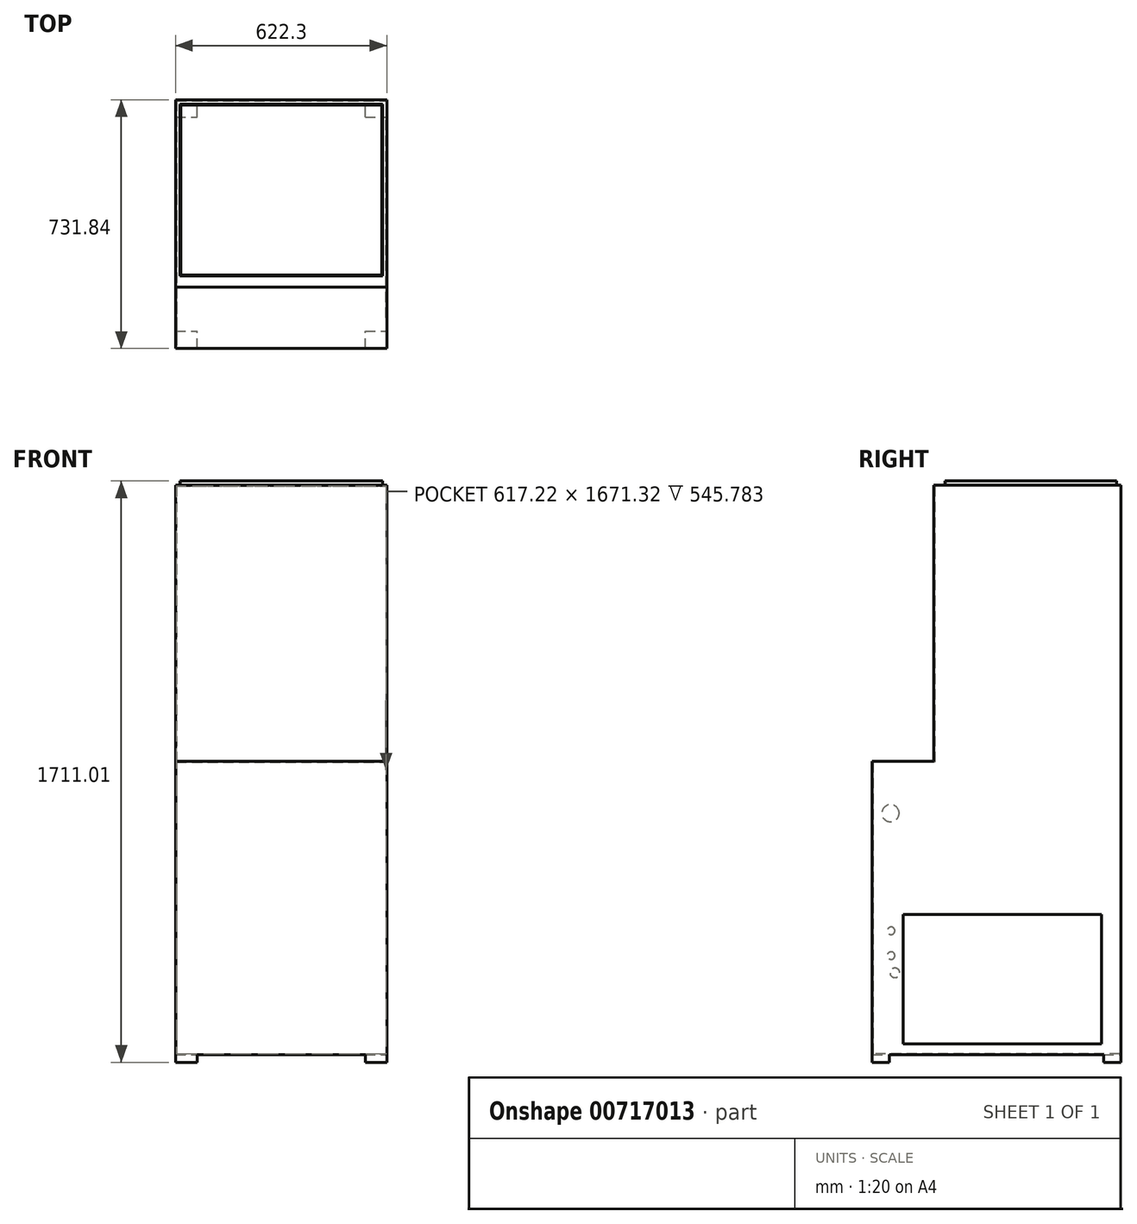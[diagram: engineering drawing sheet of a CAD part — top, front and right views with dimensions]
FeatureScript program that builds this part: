
annotation { "Feature Type Name" : "Feature", "Feature Type Description" : "" }
export const myFeature = defineFeature(function(context is Context, id is Id, definition is map)
    precondition{}
    {
        {
            var Q0;
            Q0=qCreatedBy(makeId("Top.planeOp"),FACE);
            var sketch = newSketch(context, id + "F0", { "sketchPlane" : qUnion([Q0])});
            skLineSegment(sketch, "E0.bottom", {"start": v(-311.15, 365.92) * mm, "end": v(311.15, 365.92) * mm});
            skLineSegment(sketch, "E0.top", {"start": v(-311.15, -365.92) * mm, "end": v(311.15, -365.92) * mm});
            skLineSegment(sketch, "E0.left", {"start": v(-311.15, 365.92) * mm, "end": v(-311.15, -365.92) * mm});
            skLineSegment(sketch, "E0.right", {"start": v(311.15, 365.92) * mm, "end": v(311.15, -365.92) * mm});
            skLineSegment(sketch, "E1", {"start": v(0, 0) * mm, "end": v(-311.15, 0) * mm, "construction": true});
            skLineSegment(sketch, "E2", {"start": v(0, 0) * mm, "end": v(0, 365.92) * mm, "construction": true});
            skSolve(sketch);
        }
        {
            var Q0;
            Q0=makeQuery(id+"F0.imprint","IMPRINT",FACE,{"disambiguationData":[TD([[makeQuery(id+"F0.imprint","IMPRINT",EDGE,{"derivedFrom":sQuery(id+"F0.wireOp",EDGE,"E0.bottom")}),-1.0]])]});
            extrude(context, id + "F1", {"entities" : qUnion([Q0]), "depth" : 863.6 * mm, "offsetDistance" : 25.4 * mm});
        }
        {
            var Q0;
            Q0=makeQuery(id+"F1.opExtrude","CAP_FACE",FACE,{"disambiguationData":[OSD([sQuery(id+"F0.wireOp",EDGE,"E0.bottom"),sQuery(id+"F0.wireOp",EDGE,"E0.top"),sQuery(id+"F0.wireOp",EDGE,"E0.left"),sQuery(id+"F0.wireOp",EDGE,"E0.right")])],"isStart":false});
            var sketch = newSketch(context, id + "F2", { "sketchPlane" : qUnion([Q0])});
            skLineSegment(sketch, "E3.bottom", {"start": v(-311.15, 365.92) * mm, "end": v(311.15, 365.92) * mm});
            skLineSegment(sketch, "E3.top", {"start": v(-311.15, -184.94) * mm, "end": v(311.15, -184.94) * mm});
            skLineSegment(sketch, "E3.left", {"start": v(-311.15, 365.92) * mm, "end": v(-311.15, -184.94) * mm});
            skLineSegment(sketch, "E3.right", {"start": v(311.15, 365.92) * mm, "end": v(311.15, -184.94) * mm});
            skSolve(sketch);
        }
        {
            var Q0;
            Q0=makeQuery(id+"F2.imprint","IMPRINT",FACE,{"disambiguationData":[TD([[makeQuery(id+"F2.imprint","IMPRINT",EDGE,{"derivedFrom":sQuery(id+"F2.wireOp",EDGE,"E3.bottom")}),-1.0]])]});
            extrude(context, id + "F3", {"entities" : qUnion([Q0]), "operationType" : NewBodyOperationType.ADD, "depth" : 812.8 * mm, "offsetDistance" : 25.4 * mm});
        }
        {
            var Q0;
            Q0=makeQuery(id+"F3.opExtrude","CAP_FACE",FACE,{"disambiguationData":[OSD([sQuery(id+"F2.wireOp",EDGE,"E3.bottom"),sQuery(id+"F2.wireOp",EDGE,"E3.top"),sQuery(id+"F2.wireOp",EDGE,"E3.left"),sQuery(id+"F2.wireOp",EDGE,"E3.right")])],"isStart":false});
            var sketch = newSketch(context, id + "F4", { "sketchPlane" : qUnion([Q0])});
            skLineSegment(sketch, "E4.bottom", {"start": v(-298.45, 353.22) * mm, "end": v(298.45, 353.22) * mm});
            skLineSegment(sketch, "E4.top", {"start": v(-298.45, -151.6) * mm, "end": v(298.45, -151.6) * mm});
            skLineSegment(sketch, "E4.left", {"start": v(-298.45, 353.22) * mm, "end": v(-298.45, -151.6) * mm});
            skLineSegment(sketch, "E4.right", {"start": v(298.45, 353.22) * mm, "end": v(298.45, -151.6) * mm});
            skLineSegment(sketch, "E5.0", {"start": v(295.91, 350.68) * mm, "end": v(295.91, -149.07) * mm});
            skLineSegment(sketch, "E5.1", {"start": v(-295.91, 350.68) * mm, "end": v(295.91, 350.68) * mm});
            skLineSegment(sketch, "E5.2", {"start": v(-295.91, 350.68) * mm, "end": v(-295.91, -149.07) * mm});
            skLineSegment(sketch, "E5.3", {"start": v(-295.91, -149.07) * mm, "end": v(295.91, -149.07) * mm});
            skSolve(sketch);
        }
        {
            var Q0;
            Q0=makeQuery(id+"F4.imprint","IMPRINT",FACE,{"disambiguationData":[TD([[makeQuery(id+"F4.imprint","IMPRINT",EDGE,{"derivedFrom":sQuery(id+"F4.wireOp",EDGE,"E4.bottom")}),-1.0]])]});
            extrude(context, id + "F5", {"entities" : qUnion([Q0]), "operationType" : NewBodyOperationType.ADD, "depth" : 12.7 * mm, "offsetDistance" : 25.4 * mm});
        }
        {
            var Q0;
            Q0=makeQuery(id+"F5.boolean.opBoolean","SPLIT",FACE,{"disambiguationData":[TD([makeQuery(id+"F5.opExtrude","SWEPT_FACE",FACE,{"disambiguationData":[OSD([sQuery(id+"F4.wireOp",EDGE,"E5.0")])]})])],"derivedFrom":makeQuery(id+"F3.opExtrude","CAP_FACE",FACE,{"disambiguationData":[OSD([sQuery(id+"F2.wireOp",EDGE,"E3.bottom"),sQuery(id+"F2.wireOp",EDGE,"E3.top"),sQuery(id+"F2.wireOp",EDGE,"E3.left"),sQuery(id+"F2.wireOp",EDGE,"E3.right")])],"isStart":false})});
            shell(context, id + "F6", {"entities" : qUnion([Q0]), "thickness" : 2.54 * mm});
        }
        {
            var Q0;
            Q0=makeQuery(id+"F3.boolean.opBoolean","MERGE",FACE,{"derivedFrom":[makeQuery(id+"F1.opExtrude","SWEPT_FACE",FACE,{"disambiguationData":[OSD([sQuery(id+"F0.wireOp",EDGE,"E0.left")])]}),makeQuery(id+"F3.opExtrude","SWEPT_FACE",FACE,{"disambiguationData":[OSD([sQuery(id+"F2.wireOp",EDGE,"E3.left")])]})]});
            var sketch = newSketch(context, id + "F7", { "sketchPlane" : qUnion([Q0])});
            skCircle(sketch, "E6", {"center": v(310.36, 365.13) * mm, "radius": 11.11 * mm});
            skCircle(sketch, "E7", {"center": v(310.36, 292.1) * mm, "radius": 11.11 * mm});
            skCircle(sketch, "E8", {"center": v(299.24, 241.3) * mm, "radius": 14.29 * mm});
            skCircle(sketch, "E9", {"center": v(311.94, 711.2) * mm, "radius": 25.4 * mm});
            skSolve(sketch);
        }
        {
            var Q0;
            Q0 = qSketchRegion(id + "F7", true);
            extrude(context, id + "F8", {"entities" : qUnion([Q0]), "operationType" : NewBodyOperationType.REMOVE, "oppositeDirection" : true, "depth" : 2.54 * mm, "offsetDistance" : 25.4 * mm});
        }
        {
            var Q0;
            Q0=makeQuery(id+"F3.boolean.opBoolean","MERGE",FACE,{"derivedFrom":[makeQuery(id+"F1.opExtrude","SWEPT_FACE",FACE,{"disambiguationData":[OSD([sQuery(id+"F0.wireOp",EDGE,"E0.right")])]}),makeQuery(id+"F3.opExtrude","SWEPT_FACE",FACE,{"disambiguationData":[OSD([sQuery(id+"F2.wireOp",EDGE,"E3.right")])]})]});
            var sketch = newSketch(context, id + "F9", { "sketchPlane" : qUnion([Q0])});
            skLineSegment(sketch, "E10.bottom", {"start": v(-275.43, 412.75) * mm, "end": v(308.77, 412.75) * mm});
            skLineSegment(sketch, "E10.top", {"start": v(-275.43, 31.75) * mm, "end": v(308.77, 31.75) * mm});
            skLineSegment(sketch, "E10.left", {"start": v(-275.43, 412.75) * mm, "end": v(-275.43, 31.75) * mm});
            skLineSegment(sketch, "E10.right", {"start": v(308.77, 412.75) * mm, "end": v(308.77, 31.75) * mm});
            skSolve(sketch);
        }
        {
            var Q0;
            Q0 = qSketchRegion(id + "F9", true);
            var Q1;
            Q1=makeQuery(id+"F3.boolean.opBoolean","MERGE",FACE,{"derivedFrom":[makeQuery(id+"F1.opExtrude","SWEPT_FACE",FACE,{"disambiguationData":[OSD([sQuery(id+"F0.wireOp",EDGE,"E0.left")])]}),makeQuery(id+"F3.opExtrude","SWEPT_FACE",FACE,{"disambiguationData":[OSD([sQuery(id+"F2.wireOp",EDGE,"E3.left")])]})]});
            extrude(context, id + "F10", {"entities" : qUnion([Q0, Q1]), "operationType" : NewBodyOperationType.REMOVE, "oppositeDirection" : true, "depth" : 622.3 * mm, "offsetDistance" : 25.4 * mm});
        }
        {
            var Q0;
            Q0=makeQuery(id+"F1.opExtrude","CAP_FACE",FACE,{"disambiguationData":[OSD([sQuery(id+"F0.wireOp",EDGE,"E0.bottom"),sQuery(id+"F0.wireOp",EDGE,"E0.top"),sQuery(id+"F0.wireOp",EDGE,"E0.left"),sQuery(id+"F0.wireOp",EDGE,"E0.right")])],"isStart":true});
            var sketch = newSketch(context, id + "F11", { "sketchPlane" : qUnion([Q0])});
            skLineSegment(sketch, "E11.bottom", {"start": v(-311.15, 365.92) * mm, "end": v(-247.65, 365.92) * mm});
            skLineSegment(sketch, "E11.top", {"start": v(-311.15, 315.12) * mm, "end": v(-247.65, 315.12) * mm});
            skLineSegment(sketch, "E11.left", {"start": v(-311.15, 365.92) * mm, "end": v(-311.15, 315.12) * mm});
            skLineSegment(sketch, "E11.right", {"start": v(-247.65, 365.92) * mm, "end": v(-247.65, 315.12) * mm});
            skLineSegment(sketch, "E12.0.1.0", {"start": v(-311.15, -315.12) * mm, "end": v(-311.15, -365.92) * mm});
            skLineSegment(sketch, "E12.0.1.1", {"start": v(-311.15, -315.12) * mm, "end": v(-247.65, -315.12) * mm});
            skLineSegment(sketch, "E12.0.1.2", {"start": v(-311.15, -365.92) * mm, "end": v(-247.65, -365.92) * mm});
            skLineSegment(sketch, "E12.0.1.3", {"start": v(-247.65, -315.12) * mm, "end": v(-247.65, -365.92) * mm});
            skLineSegment(sketch, "E12.1.0.0", {"start": v(247.65, 365.92) * mm, "end": v(247.65, 315.12) * mm});
            skLineSegment(sketch, "E12.1.0.1", {"start": v(247.65, 365.92) * mm, "end": v(311.15, 365.92) * mm});
            skLineSegment(sketch, "E12.1.0.2", {"start": v(247.65, 315.12) * mm, "end": v(311.15, 315.12) * mm});
            skLineSegment(sketch, "E12.1.0.3", {"start": v(311.15, 365.92) * mm, "end": v(311.15, 315.12) * mm});
            skLineSegment(sketch, "E12.1.1.0", {"start": v(247.65, -315.12) * mm, "end": v(247.65, -365.92) * mm});
            skLineSegment(sketch, "E12.1.1.1", {"start": v(247.65, -315.12) * mm, "end": v(311.15, -315.12) * mm});
            skLineSegment(sketch, "E12.1.1.2", {"start": v(247.65, -365.92) * mm, "end": v(311.15, -365.92) * mm});
            skLineSegment(sketch, "E12.1.1.3", {"start": v(311.15, -315.12) * mm, "end": v(311.15, -365.92) * mm});
            skLineSegment(sketch, "E12.direction1", {"start": v(-311.15, 315.12) * mm, "end": v(247.65, 315.12) * mm, "construction": true});
            skLineSegment(sketch, "E12.direction2", {"start": v(-311.15, 315.12) * mm, "end": v(-311.15, -365.92) * mm, "construction": true});
            skSolve(sketch);
        }
        {
            var Q0;
            Q0 = qSketchRegion(id + "F11", true);
            extrude(context, id + "F12", {"entities" : qUnion([Q0]), "operationType" : NewBodyOperationType.ADD, "depth" : 21.9 * mm, "offsetDistance" : 25.4 * mm});
        }
    });
